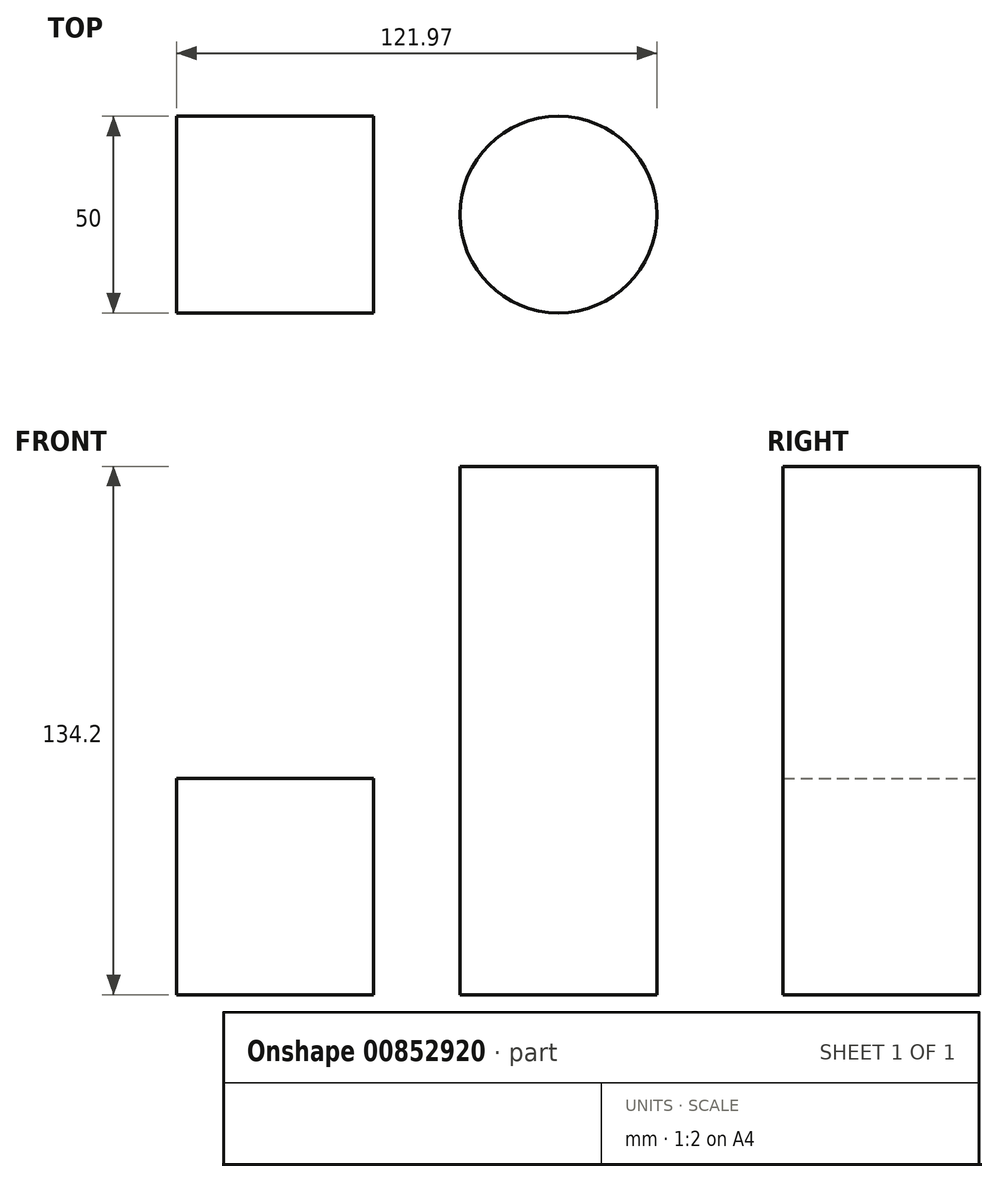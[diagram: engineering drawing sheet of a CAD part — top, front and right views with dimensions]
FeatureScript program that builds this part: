
annotation { "Feature Type Name" : "Feature", "Feature Type Description" : "" }
export const myFeature = defineFeature(function(context is Context, id is Id, definition is map)
    precondition{}
    {
        {
            var Q0;
            Q0=qCreatedBy(makeId("Top.planeOp"),FACE);
            var sketch = newSketch(context, id + "F0", { "sketchPlane" : qUnion([Q0])});
            skLineSegment(sketch, "E0.bottom", {"start": v(-25, -25) * mm, "end": v(25, -25) * mm});
            skLineSegment(sketch, "E0.top", {"start": v(-25, 25) * mm, "end": v(25, 25) * mm});
            skLineSegment(sketch, "E0.left", {"start": v(-25, -25) * mm, "end": v(-25, 25) * mm});
            skLineSegment(sketch, "E0.right", {"start": v(25, -25) * mm, "end": v(25, 25) * mm});
            skPoint(sketch, "E0.middle", {"position": v(0, 0) * mm});
            skCircle(sketch, "E1", {"center": v(71.97, 0) * mm, "radius": 25 * mm});
            skSolve(sketch);
        }
        {
            var Q0;
            Q0=makeQuery(id+"F0.imprint","IMPRINT",FACE,{"disambiguationData":[TD([[makeQuery(id+"F0.imprint","IMPRINT",EDGE,{"derivedFrom":sQuery(id+"F0.wireOp",EDGE,"E0.bottom")}),1.0]])]});
            extrude(context, id + "F1", {"entities" : qUnion([Q0]), "depth" : 55 * mm, "offsetDistance" : 25 * mm});
        }
        {
            var Q0;
            Q0=makeQuery(id+"F0.imprint","IMPRINT",FACE,{"disambiguationData":[TD([[makeQuery(id+"F0.imprint","IMPRINT",EDGE,{"derivedFrom":sQuery(id+"F0.wireOp",EDGE,"E1")}),1.0]])]});
            extrude(context, id + "F2", {"entities" : qUnion([Q0]), "depth" : 134.2 * mm, "offsetDistance" : 25 * mm});
        }
    });
